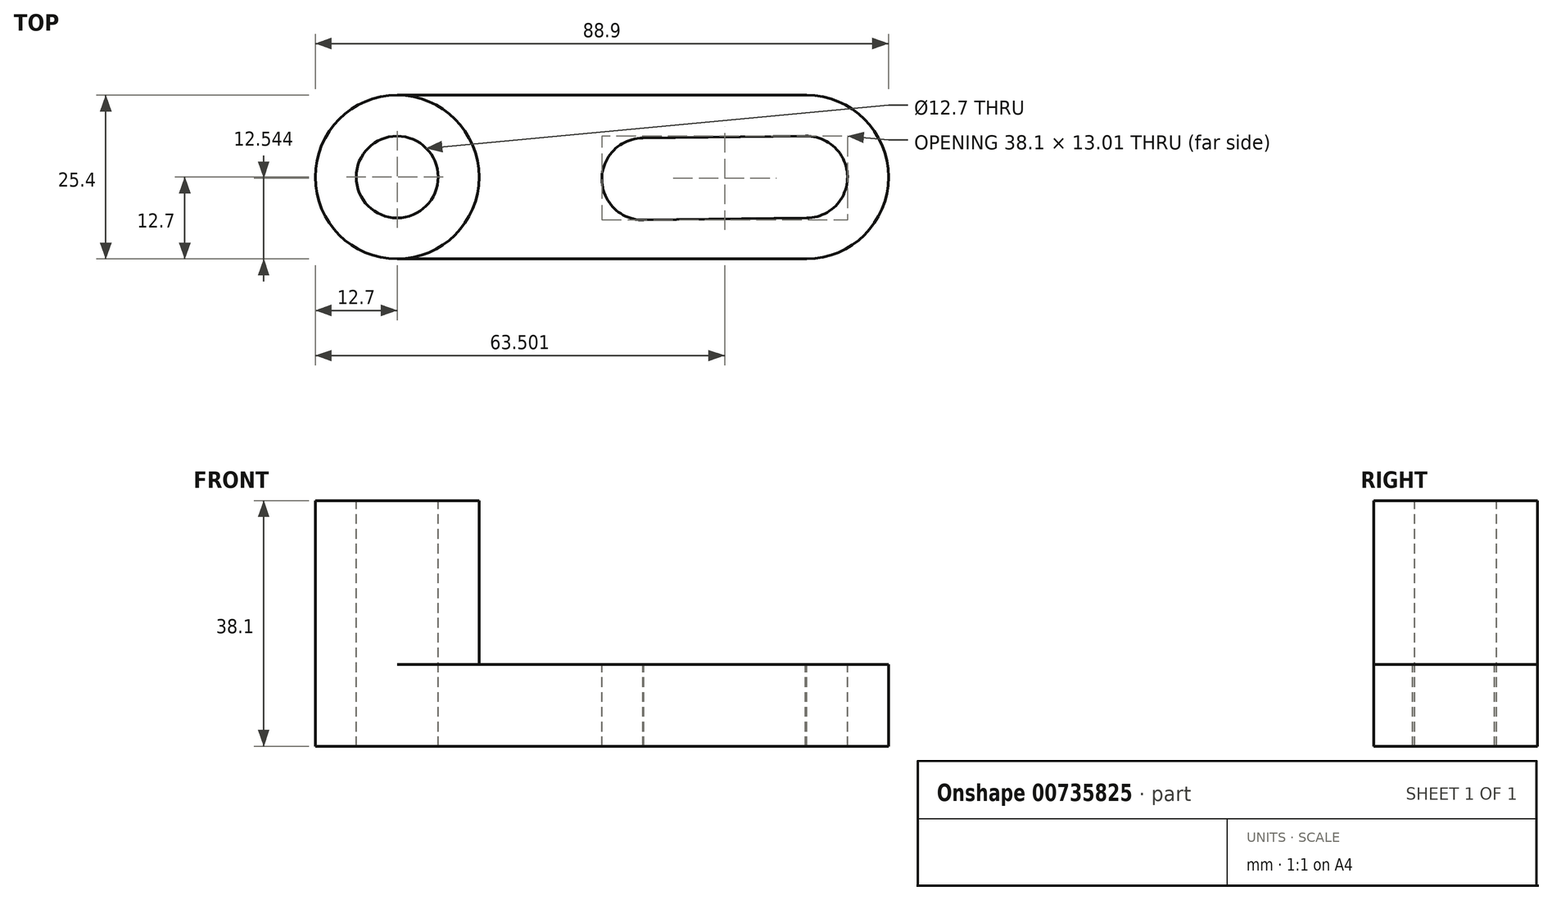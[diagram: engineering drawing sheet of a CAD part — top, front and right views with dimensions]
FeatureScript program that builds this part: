
annotation { "Feature Type Name" : "Feature", "Feature Type Description" : "" }
export const myFeature = defineFeature(function(context is Context, id is Id, definition is map)
    precondition{}
    {
        {
            var Q0;
            Q0=qCreatedBy(makeId("Top.planeOp"),FACE);
            var sketch = newSketch(context, id + "F0", { "sketchPlane" : qUnion([Q0])});
            skLineSegment(sketch, "E0", {"start": v(0, 0) * mm, "end": v(0, 25.4) * mm});
            skLineSegment(sketch, "E1", {"start": v(0, 25.4) * mm, "end": v(63.5, 25.4) * mm});
            skLineSegment(sketch, "E2", {"start": v(63.5, 25.4) * mm, "end": v(63.5, 0) * mm});
            skLineSegment(sketch, "E3", {"start": v(63.5, 0) * mm, "end": v(0, 0) * mm});
            skCircle(sketch, "E4", {"center": v(0, 12.7) * mm, "radius": 12.7 * mm});
            skCircle(sketch, "E5", {"center": v(63.5, 12.7) * mm, "radius": 12.7 * mm});
            skSolve(sketch);
        }
        {
            var Q0;
            Q0 = qSketchRegion(id + "F0", true);
            extrude(context, id + "F1", {"entities" : qUnion([Q0]), "depth" : 12.7 * mm, "offsetDistance" : 25.4 * mm});
        }
        {
            var Q0;
            Q0=makeQuery(id+"F1.opExtrude","CAP_FACE",FACE,{"disambiguationData":[OSD([sQuery(id+"F0.wireOp",EDGE,"E1"),sQuery(id+"F0.wireOp",EDGE,"E3"),sQuery(id+"F0.wireOp",EDGE,"E4"),sQuery(id+"F0.wireOp",EDGE,"E5")])],"isStart":false});
            var sketch = newSketch(context, id + "F2", { "sketchPlane" : qUnion([Q0])});
            skCircle(sketch, "E6", {"center": v(0, 12.7) * mm, "radius": 12.7 * mm});
            skSolve(sketch);
        }
        {
            var Q0;
            Q0 = qSketchRegion(id + "F2", true);
            extrude(context, id + "F3", {"entities" : qUnion([Q0]), "operationType" : NewBodyOperationType.ADD, "depth" : 25.4 * mm, "offsetDistance" : 25.4 * mm});
        }
        {
            var Q0;
            Q0=makeQuery(id+"F3.opExtrude","CAP_FACE",FACE,{"disambiguationData":[OSD([sQuery(id+"F2.wireOp",EDGE,"E6")])],"isStart":false});
            var sketch = newSketch(context, id + "F4", { "sketchPlane" : qUnion([Q0])});
            skCircle(sketch, "E7", {"center": v(0, 12.7) * mm, "radius": 6.35 * mm});
            skSolve(sketch);
        }
        {
            var Q0;
            Q0 = qSketchRegion(id + "F4", true);
            extrude(context, id + "F5", {"entities" : qUnion([Q0]), "operationType" : NewBodyOperationType.REMOVE, "oppositeDirection" : true, "depth" : 38.1 * mm, "offsetDistance" : 25.4 * mm});
        }
        {
            var Q0;
            Q0=makeQuery(id+"F1.opExtrude","CAP_FACE",FACE,{"disambiguationData":[OSD([sQuery(id+"F0.wireOp",EDGE,"E1"),sQuery(id+"F0.wireOp",EDGE,"E3"),sQuery(id+"F0.wireOp",EDGE,"E4"),sQuery(id+"F0.wireOp",EDGE,"E5")])],"isStart":false});
            var sketch = newSketch(context, id + "F6", { "sketchPlane" : qUnion([Q0])});
            skCircle(sketch, "E8", {"center": v(38.1, 12.39) * mm, "radius": 6.35 * mm});
            skCircle(sketch, "E9", {"center": v(63.5, 12.7) * mm, "radius": 6.35 * mm});
            skLineSegment(sketch, "E10", {"start": v(38.1, 18.74) * mm, "end": v(38.1, 6.04) * mm});
            skLineSegment(sketch, "E11", {"start": v(38.1, 6.04) * mm, "end": v(63.5, 6.35) * mm});
            skLineSegment(sketch, "E12", {"start": v(63.5, 6.35) * mm, "end": v(63.34, 19.05) * mm});
            skLineSegment(sketch, "E13", {"start": v(63.34, 19.05) * mm, "end": v(38.1, 18.74) * mm});
            skSolve(sketch);
        }
        {
            var Q0;
            Q0 = qSketchRegion(id + "F6", true);
            extrude(context, id + "F7", {"entities" : qUnion([Q0]), "operationType" : NewBodyOperationType.REMOVE, "oppositeDirection" : true, "depth" : 12.7 * mm, "offsetDistance" : 25.4 * mm});
        }
    });
